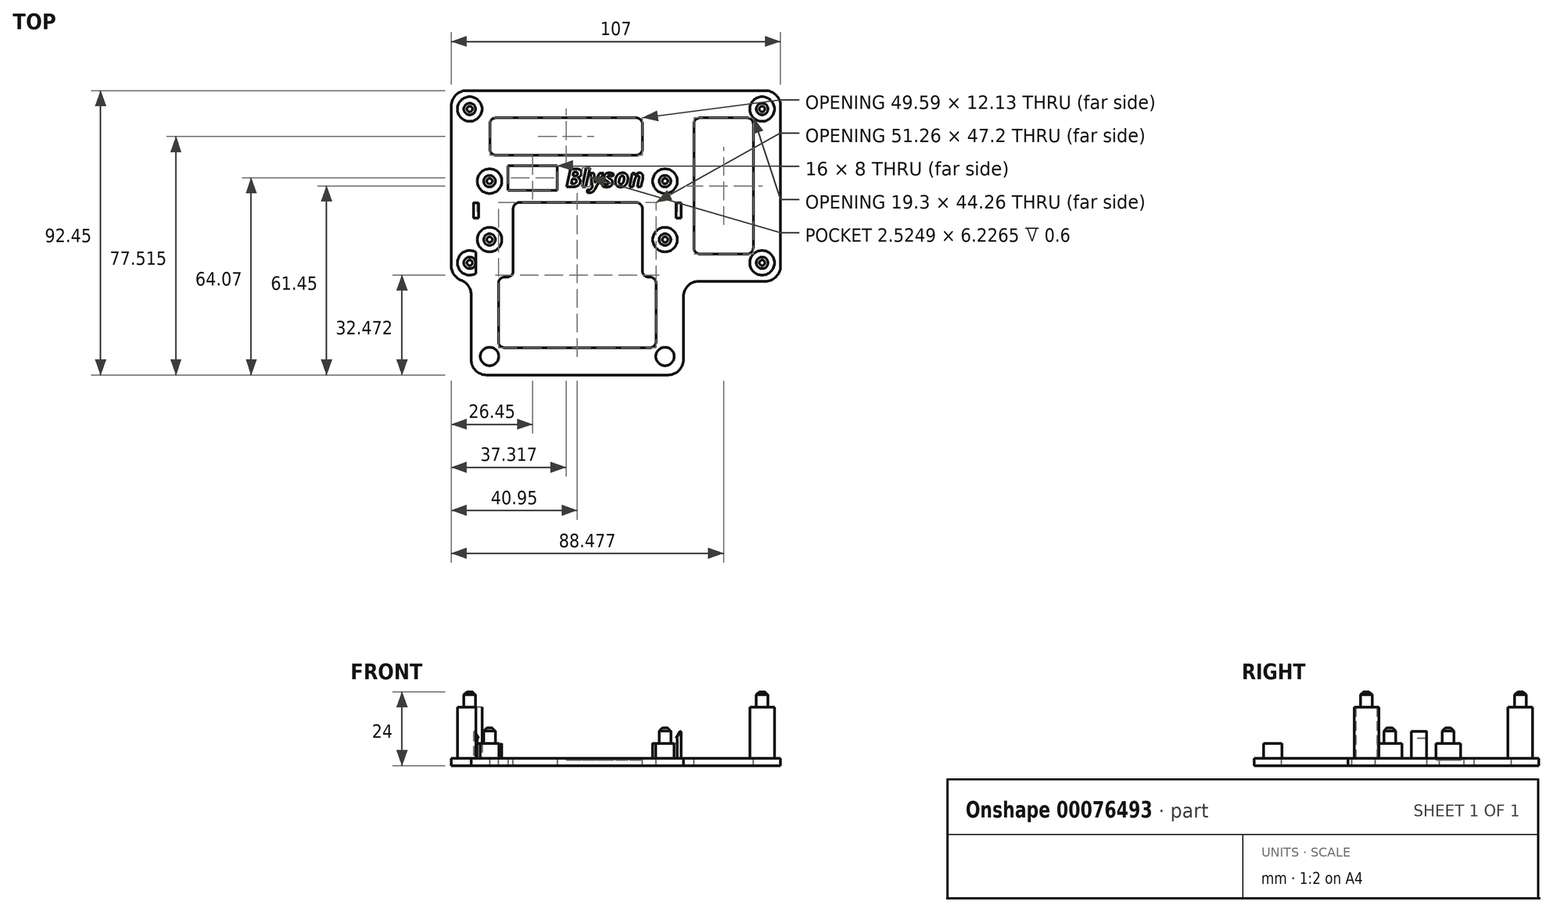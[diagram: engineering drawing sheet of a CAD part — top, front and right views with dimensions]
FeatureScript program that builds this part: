
annotation { "Feature Type Name" : "Feature", "Feature Type Description" : "" }
export const myFeature = defineFeature(function(context is Context, id is Id, definition is map)
    precondition{}
    {
        {
            var Q0;
            Q0=qCreatedBy(makeId("Top.planeOp"),FACE);
            var sketch = newSketch(context, id + "F0", { "sketchPlane" : qUnion([Q0])});
            skCircle(sketch, "E0", {"center": v(-63.45, 42.45) * mm, "radius": 2 * mm});
            skCircle(sketch, "E1", {"center": v(31.55, 42.45) * mm, "radius": 2 * mm});
            skCircle(sketch, "E2", {"center": v(31.55, -7.55) * mm, "radius": 2 * mm});
            skCircle(sketch, "E3", {"center": v(-63.45, -7.55) * mm, "radius": 2 * mm});
            skLineSegment(sketch, "E4", {"start": v(-64.1, -11.55) * mm, "end": v(62.67, -11.55) * mm, "construction": true});
            skLineSegment(sketch, "E5", {"start": v(-28.91, -9.35) * mm, "end": v(14.06, -9.35) * mm, "construction": true});
            skLineSegment(sketch, "E6", {"start": v(-55.73, 0) * mm, "end": v(19.3, 0) * mm, "construction": true});
            skLineSegment(sketch, "E7", {"start": v(0, 6.73) * mm, "end": v(0, -22.4) * mm, "construction": true});
            skCircle(sketch, "E8", {"center": v(0, 0) * mm, "radius": 2 * mm});
            skCircle(sketch, "E9", {"center": v(-57, 0) * mm, "radius": 2 * mm});
            skCircle(sketch, "E10", {"center": v(-57, 19) * mm, "radius": 2 * mm});
            skCircle(sketch, "E11", {"center": v(0, 19) * mm, "radius": 2 * mm});
            skLineSegment(sketch, "E12", {"start": v(-67.45, -11.55) * mm, "end": v(35.55, -11.55) * mm});
            skLineSegment(sketch, "E13", {"start": v(35.55, -11.55) * mm, "end": v(35.55, 46.45) * mm});
            skLineSegment(sketch, "E14", {"start": v(35.55, 46.45) * mm, "end": v(-67.45, 46.45) * mm});
            skLineSegment(sketch, "E15", {"start": v(-67.45, 46.45) * mm, "end": v(-67.45, -11.55) * mm});
            skLineSegment(sketch, "E16", {"start": v(-61, 23) * mm, "end": v(-61, -42) * mm});
            skLineSegment(sketch, "E17", {"start": v(-61, 23) * mm, "end": v(4, 23) * mm});
            skLineSegment(sketch, "E18", {"start": v(4, 23) * mm, "end": v(4, -42) * mm});
            skLineSegment(sketch, "E19", {"start": v(4, -42) * mm, "end": v(-61, -42) * mm});
            skLineSegment(sketch, "E20", {"start": v(-51, 24.07) * mm, "end": v(-51, 16.07) * mm});
            skLineSegment(sketch, "E21", {"start": v(-51, 16.07) * mm, "end": v(-35, 16.07) * mm});
            skLineSegment(sketch, "E22", {"start": v(-35, 16.07) * mm, "end": v(-35, 24.07) * mm});
            skLineSegment(sketch, "E23", {"start": v(-35, 24.07) * mm, "end": v(-51, 24.07) * mm});
            skCircle(sketch, "E24", {"center": v(-57, -38) * mm, "radius": 2 * mm});
            skCircle(sketch, "E25", {"center": v(0, -38) * mm, "radius": 2 * mm});
            skSolve(sketch);
        }
        {
            var Q0;
            Q0=qCreatedBy(makeId("Top.planeOp"),FACE);
            var sketch = newSketch(context, id + "F1", { "sketchPlane" : qUnion([Q0])});
            skLineSegment(sketch, "E26.0", {"start": v(-67.45, 46.45) * mm, "end": v(-67.45, -11.55) * mm});
            skLineSegment(sketch, "E26.1", {"start": v(35.55, 46.45) * mm, "end": v(-67.45, 46.45) * mm});
            skLineSegment(sketch, "E26.2", {"start": v(35.55, -11.55) * mm, "end": v(35.55, 46.45) * mm});
            skLineSegment(sketch, "E26.3", {"start": v(-67.45, -11.55) * mm, "end": v(-61, -11.55) * mm});
            skLineSegment(sketch, "E26.4", {"start": v(-61, -11.55) * mm, "end": v(-61, -42) * mm});
            skLineSegment(sketch, "E26.5", {"start": v(4, -42) * mm, "end": v(-61, -42) * mm});
            skLineSegment(sketch, "E26.6", {"start": v(4, -11.55) * mm, "end": v(4, -42) * mm});
            skLineSegment(sketch, "E26.7", {"start": v(-51, 16.07) * mm, "end": v(-35, 16.07) * mm});
            skLineSegment(sketch, "E26.8", {"start": v(-51, 24.07) * mm, "end": v(-51, 16.07) * mm});
            skLineSegment(sketch, "E26.9", {"start": v(-35, 24.07) * mm, "end": v(-51, 24.07) * mm});
            skLineSegment(sketch, "E26.10", {"start": v(-35, 16.07) * mm, "end": v(-35, 24.07) * mm});
            skLineSegment(sketch, "E27.trimOffspring", {"start": v(4, -11.55) * mm, "end": v(35.55, -11.55) * mm});
            skLineSegment(sketch, "E28.0", {"start": v(37.55, -13.55) * mm, "end": v(37.55, 48.45) * mm});
            skLineSegment(sketch, "E28.1", {"start": v(6, -13.55) * mm, "end": v(37.55, -13.55) * mm});
            skLineSegment(sketch, "E28.2", {"start": v(37.55, 48.45) * mm, "end": v(-69.45, 48.45) * mm});
            skLineSegment(sketch, "E28.3", {"start": v(6, -13.55) * mm, "end": v(6, -44) * mm});
            skLineSegment(sketch, "E28.4", {"start": v(-69.45, 48.45) * mm, "end": v(-69.45, -13.55) * mm});
            skLineSegment(sketch, "E28.5", {"start": v(-69.45, -13.55) * mm, "end": v(-63, -13.55) * mm});
            skLineSegment(sketch, "E28.6", {"start": v(-63, -13.55) * mm, "end": v(-63, -44) * mm});
            skLineSegment(sketch, "E28.7", {"start": v(6, -44) * mm, "end": v(-63, -44) * mm});
            skSolve(sketch);
        }
        {
            var Q0;
            Q0=makeQuery(id+"F1.imprint","IMPRINT",FACE,{"disambiguationData":[TD([[makeQuery(id+"F1.imprint","IMPRINT",EDGE,{"derivedFrom":sQuery(id+"F1.wireOp",EDGE,"E26.0")}),1.0]])]});
            var Q1;
            Q1=makeQuery(id+"F1.imprint","IMPRINT",FACE,{"disambiguationData":[TD([[makeQuery(id+"F1.imprint","IMPRINT",EDGE,{"derivedFrom":sQuery(id+"F1.wireOp",EDGE,"E26.0")}),-1.0]])]});
            extrude(context, id + "F2", {"entities" : qUnion([Q0, Q1]), "depth" : 2.4 * mm});
        }
        {
            var Q0;
            Q0=makeQuery(id+"F2.opExtrude","CAP_FACE",FACE,{"disambiguationData":[OSD([sQuery(id+"F1.wireOp",EDGE,"E26.7"),sQuery(id+"F1.wireOp",EDGE,"E26.8"),sQuery(id+"F1.wireOp",EDGE,"E26.9"),sQuery(id+"F1.wireOp",EDGE,"E26.10"),sQuery(id+"F1.wireOp",EDGE,"E28.0"),sQuery(id+"F1.wireOp",EDGE,"E28.1"),sQuery(id+"F1.wireOp",EDGE,"E28.2"),sQuery(id+"F1.wireOp",EDGE,"E28.3"),sQuery(id+"F1.wireOp",EDGE,"E28.4"),sQuery(id+"F1.wireOp",EDGE,"E28.5"),sQuery(id+"F1.wireOp",EDGE,"E28.6"),sQuery(id+"F1.wireOp",EDGE,"E28.7")])],"isStart":false});
            var sketch = newSketch(context, id + "F3", { "sketchPlane" : qUnion([Q0])});
            skCircle(sketch, "E29.0", {"center": v(-63.45, -7.55) * mm, "radius": 2 * mm});
            skCircle(sketch, "E29.1", {"center": v(-57, 0) * mm, "radius": 2 * mm});
            skCircle(sketch, "E29.2", {"center": v(-63.45, 42.45) * mm, "radius": 2 * mm});
            skCircle(sketch, "E29.3", {"center": v(31.55, 42.45) * mm, "radius": 2 * mm});
            skCircle(sketch, "E29.4", {"center": v(0, 19) * mm, "radius": 2 * mm});
            skCircle(sketch, "E29.5", {"center": v(0, 0) * mm, "radius": 2 * mm});
            skCircle(sketch, "E29.6", {"center": v(31.55, -7.55) * mm, "radius": 2 * mm});
            skCircle(sketch, "E29.7", {"center": v(0, -38) * mm, "radius": 2 * mm});
            skCircle(sketch, "E29.8", {"center": v(-57, -38) * mm, "radius": 2 * mm});
            skCircle(sketch, "E29.9", {"center": v(-57, 19) * mm, "radius": 2 * mm});
            skCircle(sketch, "E30.0", {"center": v(-63.45, 42.45) * mm, "radius": 4 * mm});
            skCircle(sketch, "E31.0", {"center": v(-57, 19) * mm, "radius": 4 * mm});
            skCircle(sketch, "E32.0", {"center": v(-57, 0) * mm, "radius": 4 * mm});
            skArc(sketch, "E33.0", {"start": v(-61.4, -4.12) * mm, "mid": v(-67.45, -7.55) * mm, "end": v(-61.4, -10.98) * mm});
            skCircle(sketch, "E34.0", {"center": v(-57, -38) * mm, "radius": 3 * mm});
            skCircle(sketch, "E35.0", {"center": v(0, -38) * mm, "radius": 3 * mm});
            skCircle(sketch, "E36.0", {"center": v(0, 0) * mm, "radius": 4 * mm});
            skCircle(sketch, "E37.0", {"center": v(0, 19) * mm, "radius": 4 * mm});
            skCircle(sketch, "E38.0", {"center": v(31.55, 42.45) * mm, "radius": 4 * mm});
            skCircle(sketch, "E39.0", {"center": v(31.55, -7.55) * mm, "radius": 4 * mm});
            skLineSegment(sketch, "E40", {"start": v(-61.4, -4.12) * mm, "end": v(-61.4, -10.98) * mm});
            skSolve(sketch);
        }
        {
            var Q0;
            Q0=makeQuery(id+"F3.imprint","IMPRINT",FACE,{"disambiguationData":[TD([[makeQuery(id+"F3.imprint","IMPRINT",EDGE,{"derivedFrom":sQuery(id+"F3.wireOp",EDGE,"E29.9")}),-1.0]])]});
            var Q1;
            Q1=makeQuery(id+"F3.imprint","IMPRINT",FACE,{"disambiguationData":[TD([[makeQuery(id+"F3.imprint","IMPRINT",EDGE,{"derivedFrom":sQuery(id+"F3.wireOp",EDGE,"E29.9")}),1.0]])]});
            var Q2;
            Q2=makeQuery(id+"F3.imprint","IMPRINT",FACE,{"disambiguationData":[TD([[makeQuery(id+"F3.imprint","IMPRINT",EDGE,{"derivedFrom":sQuery(id+"F3.wireOp",EDGE,"E29.4")}),-1.0]])]});
            var Q3;
            Q3=makeQuery(id+"F3.imprint","IMPRINT",FACE,{"disambiguationData":[TD([[makeQuery(id+"F3.imprint","IMPRINT",EDGE,{"derivedFrom":sQuery(id+"F3.wireOp",EDGE,"E29.4")}),1.0]])]});
            var Q4;
            Q4=makeQuery(id+"F3.imprint","IMPRINT",FACE,{"disambiguationData":[TD([[makeQuery(id+"F3.imprint","IMPRINT",EDGE,{"derivedFrom":sQuery(id+"F3.wireOp",EDGE,"E29.5")}),-1.0]])]});
            var Q5;
            Q5=makeQuery(id+"F3.imprint","IMPRINT",FACE,{"disambiguationData":[TD([[makeQuery(id+"F3.imprint","IMPRINT",EDGE,{"derivedFrom":sQuery(id+"F3.wireOp",EDGE,"E29.5")}),1.0]])]});
            var Q6;
            Q6=makeQuery(id+"F3.imprint","IMPRINT",FACE,{"disambiguationData":[TD([[makeQuery(id+"F3.imprint","IMPRINT",EDGE,{"derivedFrom":sQuery(id+"F3.wireOp",EDGE,"E29.1")}),-1.0]])]});
            var Q7;
            Q7=makeQuery(id+"F3.imprint","IMPRINT",FACE,{"disambiguationData":[TD([[makeQuery(id+"F3.imprint","IMPRINT",EDGE,{"derivedFrom":sQuery(id+"F3.wireOp",EDGE,"E29.1")}),1.0]])]});
            var Q8;
            Q8=makeQuery(id+"F3.imprint","IMPRINT",FACE,{"disambiguationData":[TD([[makeQuery(id+"F3.imprint","IMPRINT",EDGE,{"derivedFrom":sQuery(id+"F3.wireOp",EDGE,"E29.8")}),-1.0]])]});
            var Q9;
            Q9=makeQuery(id+"F3.imprint","IMPRINT",FACE,{"disambiguationData":[TD([[makeQuery(id+"F3.imprint","IMPRINT",EDGE,{"derivedFrom":sQuery(id+"F3.wireOp",EDGE,"E29.8")}),1.0]])]});
            var Q10;
            Q10=makeQuery(id+"F3.imprint","IMPRINT",FACE,{"disambiguationData":[TD([[makeQuery(id+"F3.imprint","IMPRINT",EDGE,{"derivedFrom":sQuery(id+"F3.wireOp",EDGE,"E29.7")}),-1.0]])]});
            var Q11;
            Q11=makeQuery(id+"F3.imprint","IMPRINT",FACE,{"disambiguationData":[TD([[makeQuery(id+"F3.imprint","IMPRINT",EDGE,{"derivedFrom":sQuery(id+"F3.wireOp",EDGE,"E29.7")}),1.0]])]});
            extrude(context, id + "F4", {"entities" : qUnion([Q0, Q1, Q2, Q3, Q4, Q5, Q6, Q7, Q8, Q9, Q10, Q11]), "operationType" : NewBodyOperationType.ADD, "depth" : 4.8 * mm});
        }
        {
            var Q0;
            Q0=makeQuery(id+"F3.imprint","IMPRINT",FACE,{"disambiguationData":[TD([[makeQuery(id+"F3.imprint","IMPRINT",EDGE,{"derivedFrom":sQuery(id+"F3.wireOp",EDGE,"E29.2")}),-1.0]])]});
            var Q1;
            Q1=makeQuery(id+"F3.imprint","IMPRINT",FACE,{"disambiguationData":[TD([[makeQuery(id+"F3.imprint","IMPRINT",EDGE,{"derivedFrom":sQuery(id+"F3.wireOp",EDGE,"E29.2")}),1.0]])]});
            var Q2;
            Q2=makeQuery(id+"F3.imprint","IMPRINT",FACE,{"disambiguationData":[TD([[makeQuery(id+"F3.imprint","IMPRINT",EDGE,{"derivedFrom":sQuery(id+"F3.wireOp",EDGE,"E29.3")}),-1.0]])]});
            var Q3;
            Q3=makeQuery(id+"F3.imprint","IMPRINT",FACE,{"disambiguationData":[TD([[makeQuery(id+"F3.imprint","IMPRINT",EDGE,{"derivedFrom":sQuery(id+"F3.wireOp",EDGE,"E29.3")}),1.0]])]});
            var Q4;
            Q4=makeQuery(id+"F3.imprint","IMPRINT",FACE,{"disambiguationData":[TD([[makeQuery(id+"F3.imprint","IMPRINT",EDGE,{"derivedFrom":sQuery(id+"F3.wireOp",EDGE,"E29.6")}),-1.0]])]});
            var Q5;
            Q5=makeQuery(id+"F3.imprint","IMPRINT",FACE,{"disambiguationData":[TD([[makeQuery(id+"F3.imprint","IMPRINT",EDGE,{"derivedFrom":sQuery(id+"F3.wireOp",EDGE,"E29.6")}),1.0]])]});
            var Q6;
            Q6=makeQuery(id+"F3.imprint","IMPRINT",FACE,{"disambiguationData":[TD([[makeQuery(id+"F3.imprint","IMPRINT",EDGE,{"derivedFrom":sQuery(id+"F3.wireOp",EDGE,"E29.0")}),-1.0]])]});
            var Q7;
            Q7=makeQuery(id+"F3.imprint","IMPRINT",FACE,{"disambiguationData":[TD([[makeQuery(id+"F3.imprint","IMPRINT",EDGE,{"derivedFrom":sQuery(id+"F3.wireOp",EDGE,"E29.0")}),1.0]])]});
            extrude(context, id + "F5", {"entities" : qUnion([Q0, Q1, Q2, Q3, Q4, Q5, Q6, Q7]), "operationType" : NewBodyOperationType.ADD, "depth" : 16.6 * mm});
        }
        {
            var Q0;
            Q0=makeQuery(id+"F4.opExtrude","CAP_FACE",FACE,{"disambiguationData":[OSD([sQuery(id+"F3.wireOp",EDGE,"E31.0")])],"isStart":false});
            var sketch = newSketch(context, id + "F6", { "sketchPlane" : qUnion([Q0])});
            skCircle(sketch, "E41.0", {"center": v(-57, 19) * mm, "radius": 2 * mm});
            skCircle(sketch, "E41.1", {"center": v(-57, 0) * mm, "radius": 2 * mm});
            skCircle(sketch, "E41.2", {"center": v(0, 19) * mm, "radius": 2 * mm});
            skCircle(sketch, "E41.3", {"center": v(0, 0) * mm, "radius": 2 * mm});
            skCircle(sketch, "E42.0", {"center": v(-57, 19) * mm, "radius": 1.9 * mm});
            skCircle(sketch, "E43.0", {"center": v(0, 19) * mm, "radius": 1.9 * mm});
            skCircle(sketch, "E44.0", {"center": v(0, 0) * mm, "radius": 1.9 * mm});
            skCircle(sketch, "E45.0", {"center": v(-57, 0) * mm, "radius": 1.9 * mm});
            skSolve(sketch);
        }
        {
            var Q0;
            Q0=makeQuery(id+"F6.imprint","IMPRINT",FACE,{"disambiguationData":[TD([[makeQuery(id+"F6.imprint","IMPRINT",EDGE,{"derivedFrom":sQuery(id+"F6.wireOp",EDGE,"E45.0")}),1.0]])]});
            var Q1;
            Q1=makeQuery(id+"F6.imprint","IMPRINT",FACE,{"disambiguationData":[TD([[makeQuery(id+"F6.imprint","IMPRINT",EDGE,{"derivedFrom":sQuery(id+"F6.wireOp",EDGE,"E42.0")}),1.0]])]});
            var Q2;
            Q2=makeQuery(id+"F6.imprint","IMPRINT",FACE,{"disambiguationData":[TD([[makeQuery(id+"F6.imprint","IMPRINT",EDGE,{"derivedFrom":sQuery(id+"F6.wireOp",EDGE,"E43.0")}),1.0]])]});
            var Q3;
            Q3=makeQuery(id+"F6.imprint","IMPRINT",FACE,{"disambiguationData":[TD([[makeQuery(id+"F6.imprint","IMPRINT",EDGE,{"derivedFrom":sQuery(id+"F6.wireOp",EDGE,"E44.0")}),1.0]])]});
            extrude(context, id + "F7", {"entities" : qUnion([Q0, Q1, Q2, Q3]), "operationType" : NewBodyOperationType.ADD, "depth" : 5 * mm});
        }
        {
            var Q0;
            Q0=makeQuery(id+"F5.opExtrude","CAP_FACE",FACE,{"disambiguationData":[OSD([sQuery(id+"F3.wireOp",EDGE,"E30.0")])],"isStart":false});
            var sketch = newSketch(context, id + "F8", { "sketchPlane" : qUnion([Q0])});
            skCircle(sketch, "E46.0", {"center": v(-63.45, 42.45) * mm, "radius": 2 * mm});
            skCircle(sketch, "E46.1", {"center": v(-63.45, -7.55) * mm, "radius": 2 * mm});
            skCircle(sketch, "E46.2", {"center": v(31.55, -7.55) * mm, "radius": 2 * mm});
            skCircle(sketch, "E46.3", {"center": v(31.55, 42.45) * mm, "radius": 2 * mm});
            skCircle(sketch, "E47.0", {"center": v(-63.45, 42.45) * mm, "radius": 1.9 * mm});
            skCircle(sketch, "E48.0", {"center": v(31.55, 42.45) * mm, "radius": 1.9 * mm});
            skCircle(sketch, "E49.0", {"center": v(-63.45, -7.55) * mm, "radius": 1.9 * mm});
            skCircle(sketch, "E50.0", {"center": v(31.55, -7.55) * mm, "radius": 1.9 * mm});
            skSolve(sketch);
        }
        {
            var Q0;
            Q0=makeQuery(id+"F8.imprint","IMPRINT",FACE,{"disambiguationData":[TD([[makeQuery(id+"F8.imprint","IMPRINT",EDGE,{"derivedFrom":sQuery(id+"F8.wireOp",EDGE,"E49.0")}),1.0]])]});
            var Q1;
            Q1=makeQuery(id+"F8.imprint","IMPRINT",FACE,{"disambiguationData":[TD([[makeQuery(id+"F8.imprint","IMPRINT",EDGE,{"derivedFrom":sQuery(id+"F8.wireOp",EDGE,"E47.0")}),1.0]])]});
            var Q2;
            Q2=makeQuery(id+"F8.imprint","IMPRINT",FACE,{"disambiguationData":[TD([[makeQuery(id+"F8.imprint","IMPRINT",EDGE,{"derivedFrom":sQuery(id+"F8.wireOp",EDGE,"E48.0")}),1.0]])]});
            var Q3;
            Q3=makeQuery(id+"F8.imprint","IMPRINT",FACE,{"disambiguationData":[TD([[makeQuery(id+"F8.imprint","IMPRINT",EDGE,{"derivedFrom":sQuery(id+"F8.wireOp",EDGE,"E50.0")}),1.0]])]});
            extrude(context, id + "F9", {"entities" : qUnion([Q0, Q1, Q2, Q3]), "operationType" : NewBodyOperationType.ADD, "depth" : 5 * mm});
        }
        {
            var Q0;
            Q0=makeQuery(id+"F2.opExtrude","SWEPT_EDGE",EDGE,{"disambiguationData":[OSD([sQuery(id+"F1.wireOp",EDGE,"E28.3"),sQuery(id+"F1.wireOp",EDGE,"E28.7")])]});
            var Q1;
            Q1=makeQuery(id+"F2.opExtrude","SWEPT_EDGE",EDGE,{"disambiguationData":[OSD([sQuery(id+"F1.wireOp",EDGE,"E28.0"),sQuery(id+"F1.wireOp",EDGE,"E28.1")])]});
            var Q2;
            Q2=makeQuery(id+"F2.opExtrude","SWEPT_EDGE",EDGE,{"disambiguationData":[OSD([sQuery(id+"F1.wireOp",EDGE,"E28.6"),sQuery(id+"F1.wireOp",EDGE,"E28.7")])]});
            var Q3;
            Q3=makeQuery(id+"F2.opExtrude","SWEPT_EDGE",EDGE,{"disambiguationData":[OSD([sQuery(id+"F1.wireOp",EDGE,"E28.4"),sQuery(id+"F1.wireOp",EDGE,"E28.5")])]});
            var Q4;
            Q4=makeQuery(id+"F2.opExtrude","SWEPT_EDGE",EDGE,{"disambiguationData":[OSD([sQuery(id+"F1.wireOp",EDGE,"E28.1"),sQuery(id+"F1.wireOp",EDGE,"E28.3")])]});
            var Q5;
            Q5=makeQuery(id+"F2.opExtrude","SWEPT_EDGE",EDGE,{"disambiguationData":[OSD([sQuery(id+"F1.wireOp",EDGE,"E28.0"),sQuery(id+"F1.wireOp",EDGE,"E28.2")])]});
            var Q6;
            Q6=makeQuery(id+"F2.opExtrude","SWEPT_EDGE",EDGE,{"disambiguationData":[OSD([sQuery(id+"F1.wireOp",EDGE,"E28.2"),sQuery(id+"F1.wireOp",EDGE,"E28.4")])]});
            fillet(context, id + "F10", {"entities" : qUnion([Q0, Q1, Q2, Q3, Q4, Q5, Q6]), "radius" : 5 * mm, "tangentPropagation" : true, "allowEdgeOverflow" : false});
        }
        {
            var Q0;
            Q0=makeQuery(id+"F2.opExtrude","SWEPT_EDGE",EDGE,{"disambiguationData":[OSD([sQuery(id+"F1.wireOp",EDGE,"E28.5"),sQuery(id+"F1.wireOp",EDGE,"E28.6")])]});
            fillet(context, id + "F11", {"entities" : qUnion([Q0]), "radius" : 5 * mm, "tangentPropagation" : true, "allowEdgeOverflow" : false});
        }
        {
            var Q0;
            Q0=makeQuery(id+"F9.opExtrude","CAP_EDGE",EDGE,{"disambiguationData":[OSD([sQuery(id+"F8.wireOp",EDGE,"E50.0")])],"isStart":false});
            var Q1;
            Q1=makeQuery(id+"F7.opExtrude","CAP_EDGE",EDGE,{"disambiguationData":[OSD([sQuery(id+"F6.wireOp",EDGE,"E44.0")])],"isStart":false});
            var Q2;
            Q2=makeQuery(id+"F7.opExtrude","CAP_EDGE",EDGE,{"disambiguationData":[OSD([sQuery(id+"F6.wireOp",EDGE,"E43.0")])],"isStart":false});
            var Q3;
            Q3=makeQuery(id+"F9.opExtrude","CAP_EDGE",EDGE,{"disambiguationData":[OSD([sQuery(id+"F8.wireOp",EDGE,"E48.0")])],"isStart":false});
            var Q4;
            Q4=makeQuery(id+"F7.opExtrude","CAP_EDGE",EDGE,{"disambiguationData":[OSD([sQuery(id+"F6.wireOp",EDGE,"E42.0")])],"isStart":false});
            var Q5;
            Q5=makeQuery(id+"F9.opExtrude","CAP_EDGE",EDGE,{"disambiguationData":[OSD([sQuery(id+"F8.wireOp",EDGE,"E47.0")])],"isStart":false});
            var Q6;
            Q6=makeQuery(id+"F7.opExtrude","CAP_EDGE",EDGE,{"disambiguationData":[OSD([sQuery(id+"F6.wireOp",EDGE,"E45.0")])],"isStart":false});
            var Q7;
            Q7=makeQuery(id+"F9.opExtrude","CAP_EDGE",EDGE,{"disambiguationData":[OSD([sQuery(id+"F8.wireOp",EDGE,"E49.0")])],"isStart":false});
            chamfer(context, id + "F12", {"entities" : qUnion([Q0, Q1, Q2, Q3, Q4, Q5, Q6, Q7]), "width" : 1 * mm, "tangentPropagation" : true});
        }
        {
            var Q0;
            Q0=makeQuery(id+"F2.opExtrude","CAP_FACE",FACE,{"disambiguationData":[OSD([sQuery(id+"F1.wireOp",EDGE,"E26.7"),sQuery(id+"F1.wireOp",EDGE,"E26.8"),sQuery(id+"F1.wireOp",EDGE,"E26.9"),sQuery(id+"F1.wireOp",EDGE,"E26.10"),sQuery(id+"F1.wireOp",EDGE,"E28.0"),sQuery(id+"F1.wireOp",EDGE,"E28.1"),sQuery(id+"F1.wireOp",EDGE,"E28.2"),sQuery(id+"F1.wireOp",EDGE,"E28.3"),sQuery(id+"F1.wireOp",EDGE,"E28.4"),sQuery(id+"F1.wireOp",EDGE,"E28.5"),sQuery(id+"F1.wireOp",EDGE,"E28.6"),sQuery(id+"F1.wireOp",EDGE,"E28.7")])],"isStart":false});
            var sketch = newSketch(context, id + "F13", { "sketchPlane" : qUnion([Q0])});
            skLineSegment(sketch, "E51.0", {"start": v(-69.45, 48.45) * mm, "end": v(-69.45, -13.55) * mm});
            skLineSegment(sketch, "E51.1", {"start": v(37.55, 48.45) * mm, "end": v(-69.45, 48.45) * mm});
            skLineSegment(sketch, "E51.2", {"start": v(-69.45, -13.55) * mm, "end": v(-63, -13.55) * mm});
            skLineSegment(sketch, "E51.3", {"start": v(-63, -13.55) * mm, "end": v(-63, -44) * mm});
            skLineSegment(sketch, "E51.4", {"start": v(6, -44) * mm, "end": v(-63, -44) * mm});
            skLineSegment(sketch, "E51.5", {"start": v(6, -13.55) * mm, "end": v(6, -44) * mm});
            skLineSegment(sketch, "E51.6", {"start": v(6, -13.55) * mm, "end": v(37.55, -13.55) * mm});
            skLineSegment(sketch, "E51.7", {"start": v(37.55, -13.55) * mm, "end": v(37.55, 48.45) * mm});
            skLineSegment(sketch, "E52.0", {"start": v(-2.87, -14.2) * mm, "end": v(-2.87, -33.13) * mm});
            skLineSegment(sketch, "E52.1", {"start": v(-4.87, -35.13) * mm, "end": v(-52.13, -35.13) * mm});
            skLineSegment(sketch, "E52.2", {"start": v(11.37, -4.68) * mm, "end": v(26.68, -4.68) * mm});
            skLineSegment(sketch, "E52.3", {"start": v(-54.13, -14.2) * mm, "end": v(-54.13, -33.13) * mm});
            skLineSegment(sketch, "E52.4", {"start": v(28.68, -2.68) * mm, "end": v(28.68, 37.58) * mm});
            skLineSegment(sketch, "E52.5", {"start": v(26.68, 39.58) * mm, "end": v(11.37, 39.58) * mm});
            skLineSegment(sketch, "E53", {"start": v(-52.13, -12.2) * mm, "end": v(-51.33, -12.2) * mm});
            skLineSegment(sketch, "E54", {"start": v(9.37, -2.68) * mm, "end": v(9.37, 37.58) * mm});
            skLineSegment(sketch, "E55", {"start": v(-7.34, 37.58) * mm, "end": v(-7.34, 29.45) * mm});
            skLineSegment(sketch, "E56", {"start": v(-56.93, 29.45) * mm, "end": v(-56.93, 37.58) * mm});
            skLineSegment(sketch, "E57", {"start": v(-49.33, 10.07) * mm, "end": v(-49.33, -10.2) * mm});
            skLineSegment(sketch, "E58.trimOffspring", {"start": v(-9.34, 39.58) * mm, "end": v(-54.93, 39.58) * mm});
            skLineSegment(sketch, "E59", {"start": v(-54.93, 27.45) * mm, "end": v(-28.1, 27.45) * mm});
            skLineSegment(sketch, "E60", {"start": v(-47.33, 12.07) * mm, "end": v(-31.1, 12.07) * mm});
            skLineSegment(sketch, "E61", {"start": v(-28.1, 27.45) * mm, "end": v(-9.34, 27.45) * mm});
            skLineSegment(sketch, "E62", {"start": v(-31.1, 12.07) * mm, "end": v(-9.34, 12.07) * mm});
            skLineSegment(sketch, "E63.trimOffspring", {"start": v(-5.34, -12.2) * mm, "end": v(-4.87, -12.2) * mm});
            skLineSegment(sketch, "E64.trimOffspring", {"start": v(-7.34, 10.07) * mm, "end": v(-7.34, -10.2) * mm});
            skPoint(sketch, "E65.visualSharp", {"position": v(-56.93, 39.58) * mm});
            skArc(sketch, "E65.filletArc", {"start": v(-54.93, 39.58) * mm, "mid": v(-56.34, 39) * mm, "end": v(-56.93, 37.58) * mm});
            skPoint(sketch, "E66.visualSharp", {"position": v(-7.34, 39.58) * mm});
            skArc(sketch, "E66.filletArc", {"start": v(-7.34, 37.58) * mm, "mid": v(-7.93, 39) * mm, "end": v(-9.34, 39.58) * mm});
            skPoint(sketch, "E67.visualSharp", {"position": v(-7.34, 27.45) * mm});
            skArc(sketch, "E67.filletArc", {"start": v(-9.34, 27.45) * mm, "mid": v(-7.93, 28.04) * mm, "end": v(-7.34, 29.45) * mm});
            skPoint(sketch, "E68.visualSharp", {"position": v(-56.93, 27.45) * mm});
            skArc(sketch, "E68.filletArc", {"start": v(-56.93, 29.45) * mm, "mid": v(-56.34, 28.04) * mm, "end": v(-54.93, 27.45) * mm});
            skPoint(sketch, "E69.visualSharp", {"position": v(-49.33, 12.07) * mm});
            skArc(sketch, "E69.filletArc", {"start": v(-47.33, 12.07) * mm, "mid": v(-48.75, 11.49) * mm, "end": v(-49.33, 10.07) * mm});
            skPoint(sketch, "E70.visualSharp", {"position": v(-7.34, 12.07) * mm});
            skArc(sketch, "E70.filletArc", {"start": v(-7.34, 10.07) * mm, "mid": v(-7.93, 11.49) * mm, "end": v(-9.34, 12.07) * mm});
            skPoint(sketch, "E71.visualSharp", {"position": v(-49.33, -12.2) * mm});
            skArc(sketch, "E71.filletArc", {"start": v(-51.33, -12.2) * mm, "mid": v(-49.92, -11.62) * mm, "end": v(-49.33, -10.2) * mm});
            skPoint(sketch, "E72.visualSharp", {"position": v(-7.34, -12.2) * mm});
            skArc(sketch, "E72.filletArc", {"start": v(-7.34, -10.2) * mm, "mid": v(-6.75, -11.62) * mm, "end": v(-5.34, -12.2) * mm});
            skPoint(sketch, "E73.visualSharp", {"position": v(-2.87, -35.13) * mm});
            skArc(sketch, "E73.filletArc", {"start": v(-4.87, -35.13) * mm, "mid": v(-3.46, -34.54) * mm, "end": v(-2.87, -33.13) * mm});
            skPoint(sketch, "E74.visualSharp", {"position": v(-2.87, -12.2) * mm});
            skArc(sketch, "E74.filletArc", {"start": v(-2.87, -14.2) * mm, "mid": v(-3.46, -12.8) * mm, "end": v(-4.87, -12.2) * mm});
            skPoint(sketch, "E75.visualSharp", {"position": v(-54.13, -35.13) * mm});
            skArc(sketch, "E75.filletArc", {"start": v(-54.13, -33.13) * mm, "mid": v(-53.54, -34.54) * mm, "end": v(-52.13, -35.13) * mm});
            skPoint(sketch, "E76.visualSharp", {"position": v(9.37, 39.58) * mm});
            skArc(sketch, "E76.filletArc", {"start": v(11.37, 39.58) * mm, "mid": v(9.96, 39) * mm, "end": v(9.37, 37.58) * mm});
            skPoint(sketch, "E77.visualSharp", {"position": v(28.68, 39.58) * mm});
            skArc(sketch, "E77.filletArc", {"start": v(28.68, 37.58) * mm, "mid": v(28.1, 39) * mm, "end": v(26.68, 39.58) * mm});
            skPoint(sketch, "E78.visualSharp", {"position": v(28.68, -4.68) * mm});
            skArc(sketch, "E78.filletArc", {"start": v(26.68, -4.68) * mm, "mid": v(28.1, -4.1) * mm, "end": v(28.68, -2.68) * mm});
            skPoint(sketch, "E79.visualSharp", {"position": v(9.37, -4.68) * mm});
            skArc(sketch, "E79.filletArc", {"start": v(9.37, -2.68) * mm, "mid": v(9.96, -4.1) * mm, "end": v(11.37, -4.68) * mm});
            skPoint(sketch, "E80.visualSharp", {"position": v(-54.13, -12.2) * mm});
            skArc(sketch, "E80.filletArc", {"start": v(-52.13, -12.2) * mm, "mid": v(-53.54, -12.8) * mm, "end": v(-54.13, -14.2) * mm});
            skSolve(sketch);
        }
        {
            var Q0;
            Q0=makeQuery(id+"F13.imprint","IMPRINT",FACE,{"disambiguationData":[TD([[makeQuery(id+"F13.imprint","IMPRINT",EDGE,{"derivedFrom":sQuery(id+"F13.wireOp",EDGE,"E52.0")}),-1.0]])]});
            var Q1;
            Q1=makeQuery(id+"F13.imprint","IMPRINT",FACE,{"disambiguationData":[TD([[makeQuery(id+"F13.imprint","IMPRINT",EDGE,{"derivedFrom":sQuery(id+"F13.wireOp",EDGE,"E55")}),-1.0]])]});
            var Q2;
            Q2=makeQuery(id+"F13.imprint","IMPRINT",FACE,{"disambiguationData":[TD([[makeQuery(id+"F13.imprint","IMPRINT",EDGE,{"derivedFrom":sQuery(id+"F13.wireOp",EDGE,"E52.2")}),1.0]])]});
            extrude(context, id + "F14", {"entities" : qUnion([Q0, Q1, Q2]), "operationType" : NewBodyOperationType.REMOVE, "endBound" : BoundingType.THROUGH_ALL, "oppositeDirection" : true, "depth" : 25 * mm});
        }
        {
            var Q0;
            Q0=makeQuery(id+"F2.opExtrude","CAP_FACE",FACE,{"disambiguationData":[OSD([sQuery(id+"F1.wireOp",EDGE,"E26.7"),sQuery(id+"F1.wireOp",EDGE,"E26.8"),sQuery(id+"F1.wireOp",EDGE,"E26.9"),sQuery(id+"F1.wireOp",EDGE,"E26.10"),sQuery(id+"F1.wireOp",EDGE,"E28.0"),sQuery(id+"F1.wireOp",EDGE,"E28.1"),sQuery(id+"F1.wireOp",EDGE,"E28.2"),sQuery(id+"F1.wireOp",EDGE,"E28.3"),sQuery(id+"F1.wireOp",EDGE,"E28.4"),sQuery(id+"F1.wireOp",EDGE,"E28.5"),sQuery(id+"F1.wireOp",EDGE,"E28.6"),sQuery(id+"F1.wireOp",EDGE,"E28.7")])],"isStart":false});
            var sketch = newSketch(context, id + "F15", { "sketchPlane" : qUnion([Q0])});
            skText(sketch, "E81", { "text": "Blyson", "fontName": "NotoSans-BoldItalic.ttf"});
            const initialGuessF15  = {"E81": [-0.03214, 0.01716, 1, 0, 0.0059]};
            skSetInitialGuess(sketch, initialGuessF15);
            skSolve(sketch);
        }
        {
            var Q0;
            Q0=qSketchRegion(id+"F15",true);
            extrude(context, id + "F16", {"entities" : qUnion([Q0]), "operationType" : NewBodyOperationType.REMOVE, "oppositeDirection" : true, "depth" : 0.6 * mm});
        }
        {
            var Q0;
            {var subQ0=sQuery(id+"F1.wireOp",EDGE,"E28.4");var subQ1=sQuery(id+"F1.wireOp",EDGE,"E28.3");var subQ2=sQuery(id+"F1.wireOp",EDGE,"E28.6");var subQ3=sQuery(id+"F1.wireOp",EDGE,"E28.1");var subQ4=sQuery(id+"F1.wireOp",EDGE,"E28.2");var subQ5=sQuery(id+"F1.wireOp",EDGE,"E28.0");var subQ6=sQuery(id+"F1.wireOp",EDGE,"E26.7");var subQ7=sQuery(id+"F1.wireOp",EDGE,"E26.9");var subQ8=sQuery(id+"F1.wireOp",EDGE,"E26.10");var subQ9=sQuery(id+"F1.wireOp",EDGE,"E26.8");var subQ10=sQuery(id+"F1.wireOp",EDGE,"E28.7");var subQ11=sQuery(id+"F1.wireOp",EDGE,"E28.5");Q0=makeQuery(id+"F16.boolean.opBoolean","SPLIT",FACE,{"disambiguationData":[TD([makeQuery(id+"F2.opExtrude","SWEPT_FACE",FACE,{"disambiguationData":[OSD([subQ6])]})])],"derivedFrom":makeQuery(id+"F2.opExtrude","CAP_FACE",FACE,{"disambiguationData":[OSD([subQ6,subQ9,subQ7,subQ8,subQ5,subQ3,subQ4,subQ1,subQ0,subQ11,subQ2,subQ10])],"isStart":false})});}
            var sketch = newSketch(context, id + "F17", { "sketchPlane" : qUnion([Q0])});
            skLineSegment(sketch, "E82.0", {"start": v(-61, 23) * mm, "end": v(-61, -42) * mm, "construction": true});
            skLineSegment(sketch, "E83.0", {"start": v(4, 23) * mm, "end": v(4, -42) * mm, "construction": true});
            skLineSegment(sketch, "E84", {"start": v(-57, 19) * mm, "end": v(-57, 0) * mm, "construction": true});
            skPoint(sketch, "E85", {"position": v(-57, 9.5) * mm});
            skLineSegment(sketch, "E86", {"start": v(0, 19) * mm, "end": v(0, 0) * mm, "construction": true});
            skPoint(sketch, "E87", {"position": v(0, 9.5) * mm});
            skLineSegment(sketch, "E88", {"start": v(-57, 9.5) * mm, "end": v(0, 9.5) * mm, "construction": true});
            skPoint(sketch, "E89", {"position": v(-28.5, 9.5) * mm});
            skLineSegment(sketch, "E90", {"start": v(-61, 12) * mm, "end": v(-61, 7) * mm});
            skLineSegment(sketch, "E91", {"start": v(-61, 7) * mm, "end": v(-62.2, 7) * mm});
            skLineSegment(sketch, "E92", {"start": v(-62.2, 7) * mm, "end": v(-62.2, 12) * mm});
            skLineSegment(sketch, "E93", {"start": v(-62.2, 12) * mm, "end": v(-61, 12) * mm});
            skPoint(sketch, "E94", {"position": v(-61, 9.5) * mm});
            skLineSegment(sketch, "E95", {"start": v(-28.5, 9.5) * mm, "end": v(-28.5, 2.83) * mm, "construction": true});
            skLineSegment(sketch, "E96.MirrorCS", {"start": v(4, 7) * mm, "end": v(5.2, 7) * mm});
            skLineSegment(sketch, "E97.MirrorCS", {"start": v(4, 12) * mm, "end": v(4, 7) * mm});
            skLineSegment(sketch, "E98.MirrorCS", {"start": v(5.2, 7) * mm, "end": v(5.2, 12) * mm});
            skLineSegment(sketch, "E99.MirrorCS", {"start": v(5.2, 12) * mm, "end": v(4, 12) * mm});
            skSolve(sketch);
        }
        {
            var Q0;
            Q0=makeQuery(id+"F17.imprint","IMPRINT",FACE,{"disambiguationData":[TD([[makeQuery(id+"F17.imprint","IMPRINT",EDGE,{"derivedFrom":sQuery(id+"F17.wireOp",EDGE,"E90")}),-1.0]])]});
            var Q1;
            Q1=makeQuery(id+"F17.imprint","IMPRINT",FACE,{"disambiguationData":[TD([[makeQuery(id+"F17.imprint","IMPRINT",EDGE,{"derivedFrom":sQuery(id+"F17.wireOp",EDGE,"E96.MirrorCS")}),1.0]])]});
            extrude(context, id + "F18", {"entities" : qUnion([Q0, Q1]), "operationType" : NewBodyOperationType.ADD, "depth" : (4.8 + 1.65) * mm});
        }
        {
            var Q0;
            Q0=makeQuery(id+"F18.opExtrude","SWEPT_FACE",FACE,{"disambiguationData":[OSD([sQuery(id+"F17.wireOp",EDGE,"E91")])]});
            var sketch = newSketch(context, id + "F19", { "sketchPlane" : qUnion([Q0])});
            skLineSegment(sketch, "E100", {"start": v(-61, 8.85) * mm, "end": v(-60.6, 8.85) * mm});
            skLineSegment(sketch, "E101", {"start": v(-60.6, 8.85) * mm, "end": v(-61.83, 10.97) * mm});
            skLineSegment(sketch, "E102", {"start": v(-62.2, 10.87) * mm, "end": v(-62.2, 8.85) * mm});
            skPoint(sketch, "E103.visualSharp", {"position": v(-62.2, 11.62) * mm});
            skArc(sketch, "E103.filletArc", {"start": v(-61.83, 10.97) * mm, "mid": v(-62.05, 11.07) * mm, "end": v(-62.2, 10.87) * mm});
            skLineSegment(sketch, "E104.0", {"start": v(4, 8.85) * mm, "end": v(4, 2.4) * mm});
            skLineSegment(sketch, "E105", {"start": v(-61, 7.94) * mm, "end": v(4, 7.94) * mm, "construction": true});
            skPoint(sketch, "E106", {"position": v(-28.5, 7.94) * mm});
            skLineSegment(sketch, "E107", {"start": v(-28.5, 7.94) * mm, "end": v(-28.5, 14.75) * mm, "construction": true});
            skLineSegment(sketch, "E108", {"start": v(-62.2, 8.85) * mm, "end": v(-61, 8.85) * mm});
            skLineSegment(sketch, "E109.MirrorCS", {"start": v(5.2, 8.85) * mm, "end": v(4, 8.85) * mm});
            skLineSegment(sketch, "E110.MirrorCS", {"start": v(4, 8.85) * mm, "end": v(3.6, 8.85) * mm});
            skLineSegment(sketch, "E111.MirrorCS", {"start": v(5.2, 10.87) * mm, "end": v(5.2, 8.85) * mm});
            skLineSegment(sketch, "E112.MirrorCS", {"start": v(3.6, 8.85) * mm, "end": v(4.83, 10.97) * mm});
            skArc(sketch, "E113.MirrorCS", {"start": v(4.83, 10.97) * mm, "mid": v(5.05, 11.07) * mm, "end": v(5.2, 10.87) * mm});
            skSolve(sketch);
        }
        {
            var Q0;
            Q0=makeQuery(id+"F19.imprint","IMPRINT",FACE,{"disambiguationData":[TD([[makeQuery(id+"F19.imprint","IMPRINT",EDGE,{"derivedFrom":sQuery(id+"F19.wireOp",EDGE,"E100")}),1.0]])]});
            var Q1;
            Q1=makeQuery(id+"F19.imprint","IMPRINT",FACE,{"disambiguationData":[TD([[makeQuery(id+"F19.imprint","IMPRINT",EDGE,{"derivedFrom":sQuery(id+"F19.wireOp",EDGE,"E109.MirrorCS")}),-1.0]])]});
            var Q2;
            Q2=makeQuery(id+"F18.opExtrude","SWEPT_FACE",FACE,{"disambiguationData":[OSD([sQuery(id+"F17.wireOp",EDGE,"E93")])]});
            extrude(context, id + "F20", {"entities" : qUnion([Q0, Q1]), "operationType" : NewBodyOperationType.ADD, "endBound" : BoundingType.UP_TO_SURFACE, "oppositeDirection" : true, "endBoundEntityFace" : qUnion([Q2]), "depth" : 25 * mm});
        }
    });
